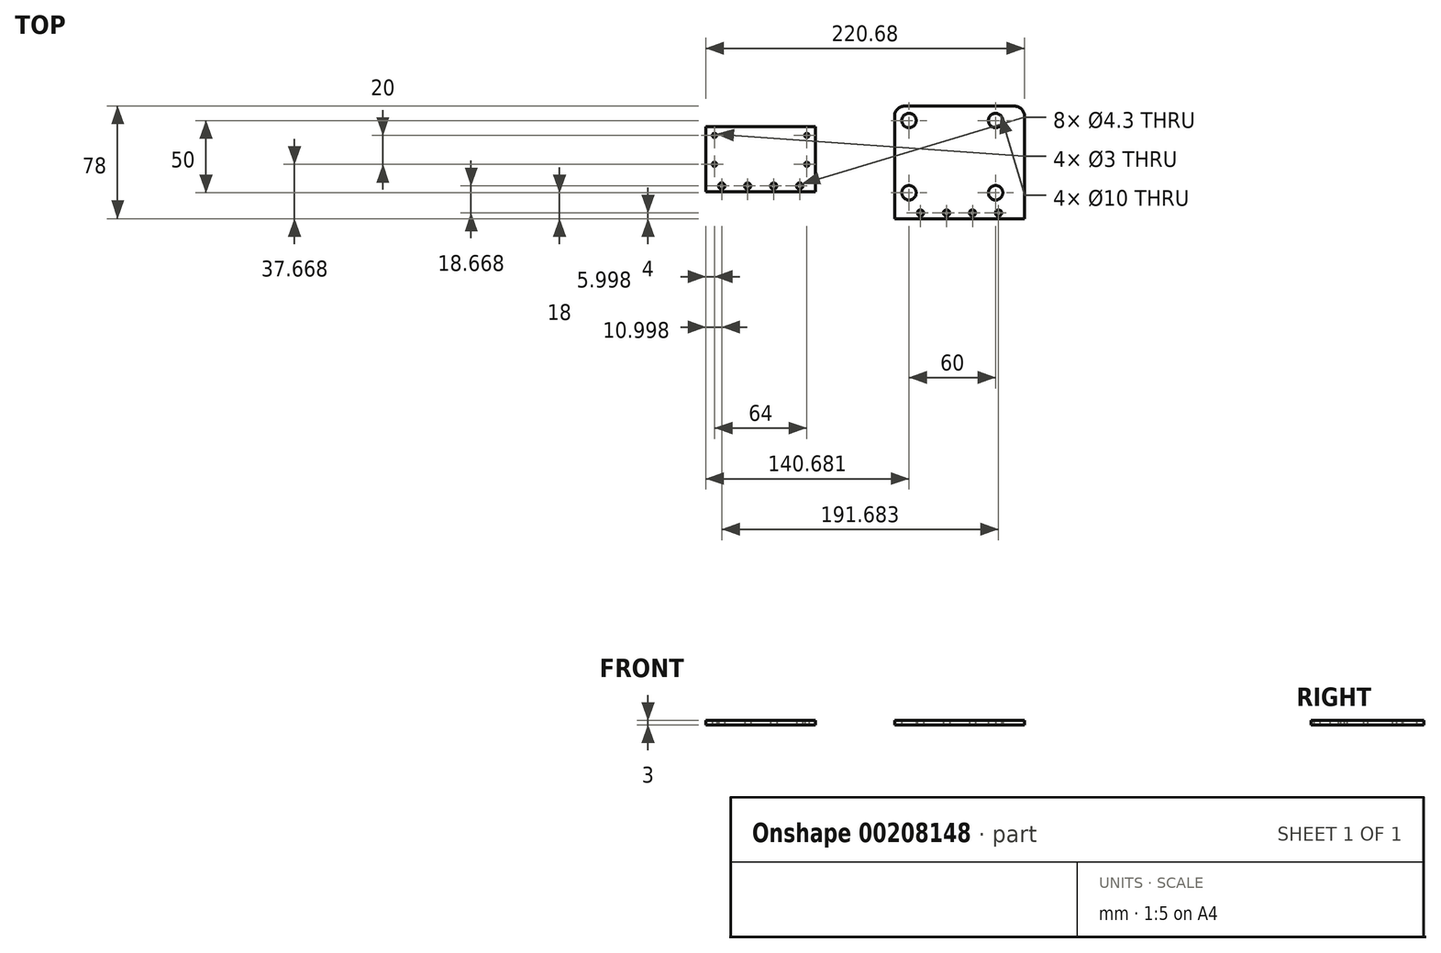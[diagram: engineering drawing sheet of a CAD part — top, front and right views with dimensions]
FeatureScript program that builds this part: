
annotation { "Feature Type Name" : "Feature", "Feature Type Description" : "" }
export const myFeature = defineFeature(function(context is Context, id is Id, definition is map)
    precondition{}
    {
        {
            var Q0;
            Q0=qCreatedBy(makeId("Top.planeOp"),FACE);
            var sketch = newSketch(context, id + "F0", { "sketchPlane" : qUnion([Q0])});
            skLineSegment(sketch, "E0", {"start": v(48.04, -30.37) * mm, "end": v(48.04, 32.63) * mm});
            skLineSegment(sketch, "E1", {"start": v(41.04, 39.63) * mm, "end": v(-34.96, 39.63) * mm});
            skLineSegment(sketch, "E2", {"start": v(-41.96, 32.63) * mm, "end": v(-41.96, -30.37) * mm});
            skCircle(sketch, "E3", {"center": v(-31.96, 29.63) * mm, "radius": 5 * mm});
            skCircle(sketch, "E4", {"center": v(-31.96, -20.37) * mm, "radius": 5 * mm});
            skCircle(sketch, "E5", {"center": v(28.04, -20.37) * mm, "radius": 5 * mm});
            skCircle(sketch, "E6", {"center": v(28.04, 29.63) * mm, "radius": 5 * mm});
            skArc(sketch, "E7", {"start": v(-34.96, 39.63) * mm, "mid": v(-39.9, 37.58) * mm, "end": v(-41.96, 32.63) * mm});
            skArc(sketch, "E8", {"start": v(48.04, 32.63) * mm, "mid": v(46, 37.58) * mm, "end": v(41.04, 39.63) * mm});
            skLineSegment(sketch, "E9", {"start": v(-41.96, -30.37) * mm, "end": v(-41.96, -38.37) * mm});
            skLineSegment(sketch, "E10", {"start": v(-41.96, -38.37) * mm, "end": v(48.04, -38.37) * mm});
            skLineSegment(sketch, "E11", {"start": v(48.04, -38.37) * mm, "end": v(48.04, -30.37) * mm});
            skCircle(sketch, "E12", {"center": v(-23.96, -34.37) * mm, "radius": 2.15 * mm});
            skCircle(sketch, "E13.1.0.0", {"center": v(-5.96, -34.37) * mm, "radius": 2.15 * mm});
            skCircle(sketch, "E13.2.0.0", {"center": v(12.04, -34.37) * mm, "radius": 2.15 * mm});
            skCircle(sketch, "E13.3.0.0", {"center": v(30.04, -34.37) * mm, "radius": 2.15 * mm});
            skSolve(sketch);
        }
        {
            var Q0;
            Q0=makeQuery(id+"F0.imprint","IMPRINT",FACE,{"disambiguationData":[TD([[makeQuery(id+"F0.imprint","IMPRINT",EDGE,{"derivedFrom":sQuery(id+"F0.wireOp",EDGE,"E0")}),1.0]])]});
            extrude(context, id + "F1", {"entities" : qUnion([Q0]), "depth" : 3 * mm});
        }
        {
            var Q0;
            Q0=qCreatedBy(makeId("Top.planeOp"),FACE);
            var sketch = newSketch(context, id + "F2", { "sketchPlane" : qUnion([Q0])});
            skLineSegment(sketch, "E14", {"start": v(-96.64, 25.3) * mm, "end": v(-172.64, 25.3) * mm});
            skCircle(sketch, "E15", {"center": v(-161.64, -15.7) * mm, "radius": 2.15 * mm});
            skCircle(sketch, "E16.1.0.0", {"center": v(-143.64, -15.7) * mm, "radius": 2.15 * mm});
            skCircle(sketch, "E16.2.0.0", {"center": v(-125.64, -15.7) * mm, "radius": 2.15 * mm});
            skCircle(sketch, "E16.3.0.0", {"center": v(-107.64, -15.7) * mm, "radius": 2.15 * mm});
            skLineSegment(sketch, "E17", {"start": v(-172.64, 25.3) * mm, "end": v(-172.64, -19.7) * mm});
            skLineSegment(sketch, "E18", {"start": v(-96.64, 25.3) * mm, "end": v(-96.64, -19.7) * mm});
            skLineSegment(sketch, "E19", {"start": v(-96.64, -19.7) * mm, "end": v(-172.64, -19.7) * mm});
            skCircle(sketch, "E20", {"center": v(-166.64, 19.3) * mm, "radius": 1.5 * mm});
            skCircle(sketch, "E21", {"center": v(-166.64, -0.7) * mm, "radius": 1.5 * mm});
            skCircle(sketch, "E22", {"center": v(-102.64, 19.3) * mm, "radius": 1.5 * mm});
            skCircle(sketch, "E23", {"center": v(-102.64, -0.7) * mm, "radius": 1.5 * mm});
            skSolve(sketch);
        }
        {
            var Q0;
            Q0=makeQuery(id+"F2.imprint","IMPRINT",FACE,{"disambiguationData":[TD([[makeQuery(id+"F2.imprint","IMPRINT",EDGE,{"derivedFrom":sQuery(id+"F2.wireOp",EDGE,"E14")}),1.0]])]});
            extrude(context, id + "F3", {"entities" : qUnion([Q0]), "depth" : 3 * mm});
        }
    });
